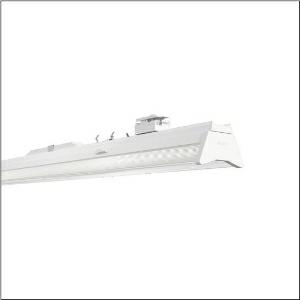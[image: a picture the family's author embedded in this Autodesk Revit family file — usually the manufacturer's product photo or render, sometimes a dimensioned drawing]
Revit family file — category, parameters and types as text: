
# Revit family: licross_r__11_performance_mo_51td16cn69xg_6612
name_source: partatom
category: Lighting Fixtures
units: mm (PartAtom-declared; Revit-internal decimal feet)

## family parameters
Cut with Voids When Loaded = No
Host = Face
Light Source = No
Part Type = Normal
Room Calculation Point = No
Round Connector Dimension = Use Diameter
Shared = No

## types (1)
- --- (1 x LED, 8960 lm, 49.4 W, 6500K)
    Apparent Load = 49 VA
    CIE Flux Codes = 66 88 96 79 100
    Color Rendering = 80
    Color Temperature = 6500K
    Default Elevation = 1800 mm
    Description = Licross® 11 Performance MO, luminaire insert, of sheet steel, galvanised, coil coated, white, length: 1.500mm, width: 120mm, height: 123mm, LED rated luminous flux: 8.960lm, light colour: 865, control gear: ON/OFF Multilumen, CLOi, with plug, 3-pole, with phase selection, mains connection: 220..240V, AC, 50/60Hz, start of lifetime: 49W, end of service life: 55W, internal wiring halogen-free, primary light control with lens, of plastic, primary optical cover: cover, of PMMA, light emission: direct/indirect distribution, primary light characteristic: symmetric, protection rating (complete): IP54, insulation class (complete): insulation class I (protective earthing), certification: CE, ENEC, VDE, UKCA, protection symbol: D if used in an environment with non-conductive dust loads with corresponding accessories, impact resistance: IK06, permissible ambient temperature for indoor applications: -35..+40°C, corresponds to IFS (International Featured Standards) requirements for safety and quality in the food industry, reducing of maximum allowable ambient temperature of 5°C with ceiling mounting, LABS conformity tested according to VDMA 24364:2018-05, packaging unit: 1 piece
    Height = 114 mm
    Lamp = 1 x LED
    Lamp Light Flux = 8960 lm
    Lamp Power = 49.4 W
    Lamp count = 1
    Length = 1500 mm
    Luminous efficacy = 181 lm/W
    Manufacturer = Siteco
    ModVariant = No
    Model = 51TD16CN69XG
    Mounting Place = Ceiling
    Mounting Type = Pendant
    Number of Poles = 1
    OnlyDefault = Yes
    Power Factor = 1
    Product Name = Licross® 11 Performance MO
    Product group = luminaire insert | ceiling pendant
    ProductGroupID = 902
    Protection Class = Protection class I
    Protection Degree = IP 54
    RLX_Detail_Level = 1
    RLX_Emergency_Light_Flux = 0 lm
    RLX_Emergency_Type = 0
    RLX_Emergency_Type_DB = No
    RlxData = <blob elided: 31869 chars, md5=7b08d016>
    Socket = socket
    Standby Power = 0 W
    System Light Flux = 8960 lm
    System Power = 49 W
    Type Comments = factory setting: luminous flux: 100 % | (A | C | E) | 113 mA
    Type Image = l_1256138.jpg
    URL = http://relux.com
    VarID = @adj_051575
    Voltage = 0 V
    Weight = 0.00 kg
    Width = 120 mm

## geometry (parser evidence)
native form markers: Blend x4, Sweep x11
no freeform markers — native parametric forms only
